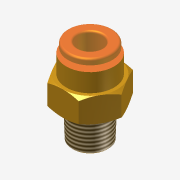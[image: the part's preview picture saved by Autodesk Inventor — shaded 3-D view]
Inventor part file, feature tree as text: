
AUTODESK INVENTOR PART (.ipt)
format: ipt  version: unknown  size: 246,272 bytes
history: native  units: mm
features: imported_body x1, thread x1
ambient origin geometry x8: Origin, YZ Plane, XZ Plane, XY Plane, X Axis, Y Axis, Z Axis, Center Point
feature tree (2):
  imported_body  "Base1"
  thread  "Thread1"  [1 undecoded]
note: 1 required parameter value undecoded (feature->parameter linkage not recoverable at this tier; creation-order binding heuristic only, values carry confidence <= 0.55)
